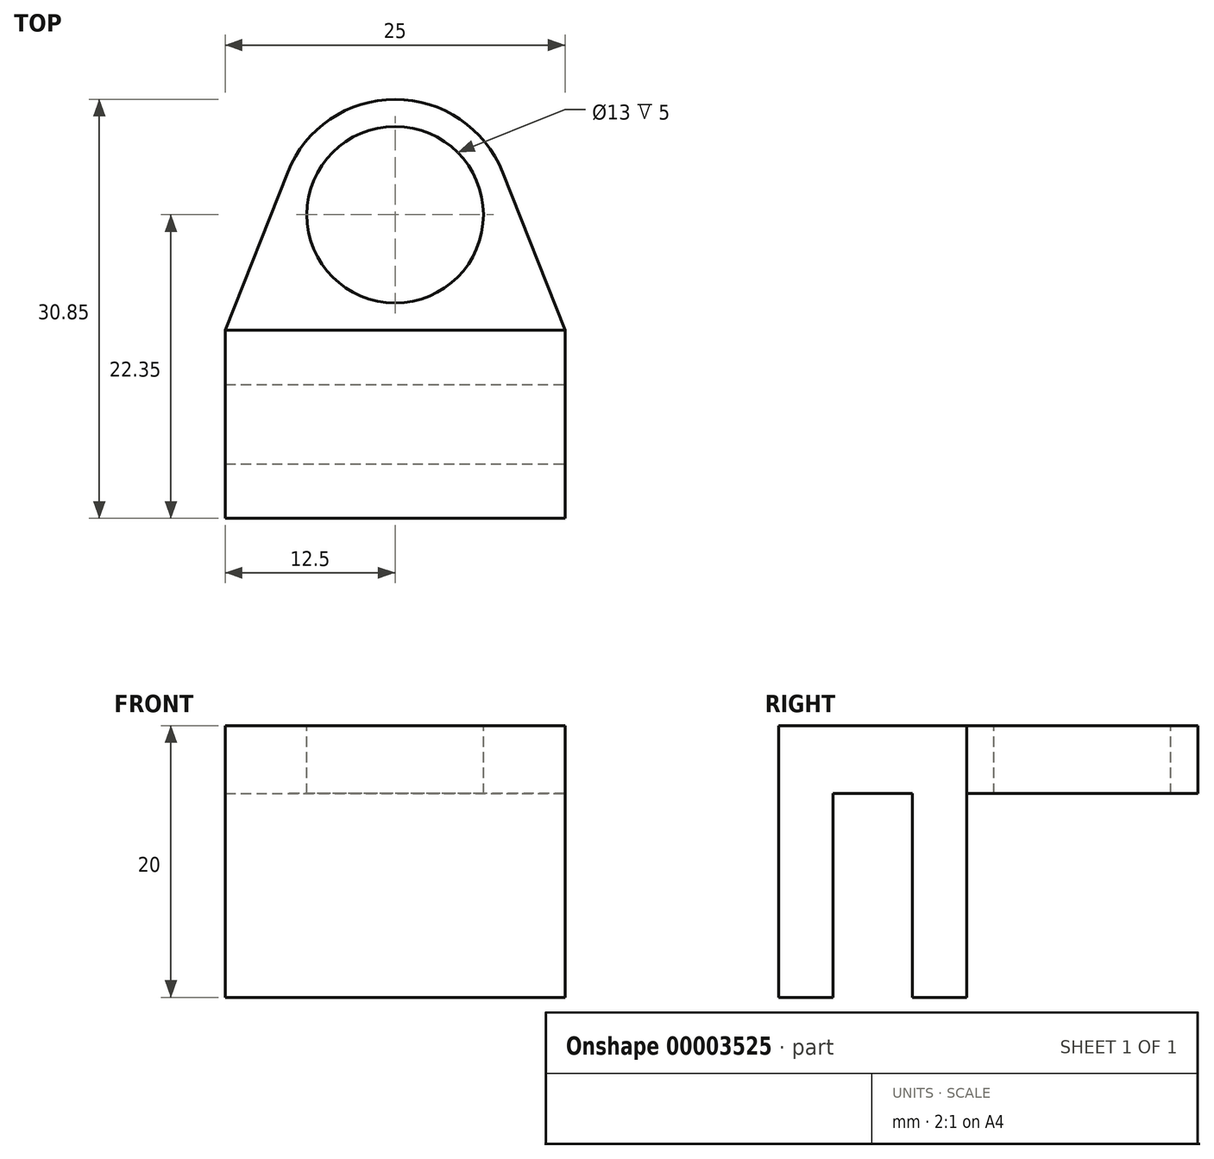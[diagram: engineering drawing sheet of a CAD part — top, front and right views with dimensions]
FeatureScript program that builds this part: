
annotation { "Feature Type Name" : "Feature", "Feature Type Description" : "" }
export const myFeature = defineFeature(function(context is Context, id is Id, definition is map)
    precondition{}
    {
        {
            var Q0;
            Q0=qCreatedBy(makeId("Right.planeOp"),FACE);
            var sketch = newSketch(context, id + "F0", { "sketchPlane" : qUnion([Q0])});
            skLineSegment(sketch, "E0", {"start": v(-13.85, 0) * mm, "end": v(-13.85, -20) * mm});
            skLineSegment(sketch, "E1", {"start": v(-13.85, -20) * mm, "end": v(-9.85, -20) * mm});
            skLineSegment(sketch, "E2", {"start": v(-9.85, -20) * mm, "end": v(-9.85, -5) * mm});
            skLineSegment(sketch, "E3", {"start": v(-9.85, -5) * mm, "end": v(-4, -5) * mm});
            skLineSegment(sketch, "E4", {"start": v(-4, -5) * mm, "end": v(-4, -20) * mm});
            skLineSegment(sketch, "E5", {"start": v(-4, -20) * mm, "end": v(0, -20) * mm});
            skLineSegment(sketch, "E6", {"start": v(0, -20) * mm, "end": v(0, 0) * mm});
            skLineSegment(sketch, "E7", {"start": v(0, 0) * mm, "end": v(-13.85, 0) * mm});
            skSolve(sketch);
        }
        {
            var Q0;
            Q0 = qSketchRegion(id + "F0", true);
            extrude(context, id + "F1", {"entities" : qUnion([Q0]), "oppositeDirection" : true, "depth" : 25 * mm});
        }
        {
            var Q0;
            Q0=qCreatedBy(makeId("Top.planeOp"),FACE);
            var sketch = newSketch(context, id + "F2", { "sketchPlane" : qUnion([Q0])});
            skCircle(sketch, "E8", {"center": v(-12.5, 8.5) * mm, "radius": 8.5 * mm});
            skLineSegment(sketch, "E9", {"start": v(0, 0) * mm, "end": v(-4.6, 11.62) * mm});
            skLineSegment(sketch, "E10", {"start": v(-25, 0) * mm, "end": v(-20.4, 11.62) * mm});
            skLineSegment(sketch, "E11", {"start": v(-25, 0) * mm, "end": v(0, 0) * mm});
            skSolve(sketch);
        }
        {
            var Q0;
            Q0 = qSketchRegion(id + "F2", true);
            extrude(context, id + "F3", {"entities" : qUnion([Q0]), "oppositeDirection" : true, "depth" : 5 * mm});
        }
        {
            var Q0;
            Q0=makeQuery(id+"F3.opExtrude","CAP_FACE",FACE,{"disambiguationData":[OSD([sQuery(id+"F2.wireOp",EDGE,"E8"),sQuery(id+"F2.wireOp",EDGE,"E9"),sQuery(id+"F2.wireOp",EDGE,"E10"),sQuery(id+"F2.wireOp",EDGE,"E11")])],"isStart":true});
            var sketch = newSketch(context, id + "F4", { "sketchPlane" : qUnion([Q0])});
            skCircle(sketch, "E12", {"center": v(-12.5, 8.5) * mm, "radius": 6.5 * mm});
            skSolve(sketch);
        }
        {
            var Q0;
            Q0 = qSketchRegion(id + "F4", true);
            extrude(context, id + "F5", {"entities" : qUnion([Q0]), "operationType" : NewBodyOperationType.REMOVE, "oppositeDirection" : true, "depth" : 25 * mm});
        }
    });
